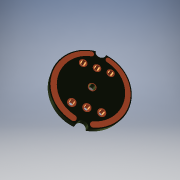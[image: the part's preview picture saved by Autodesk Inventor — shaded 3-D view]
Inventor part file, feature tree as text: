
AUTODESK INVENTOR PART (.ipt)
format: ipt  version: 2016 SP2 (Build 200237200, 237)  size: 261,632 bytes
history: native  units: mm
features: extrude x5, sketch x5, mirror x3, pattern_linear x1
ambient origin geometry x8: Origin, YZ Plane, XZ Plane, XY Plane, X Axis, Y Axis, Z Axis, Center Point
bodies: Solid1 (feature_tree), Solid2 (feature_tree), Solid3 (feature_tree), Solid4 (feature_tree)
feature tree (14):
  extrude  "Extrusion1"  Depth=10.0mm
  extrude  "Extrusion2"  Depth=1.4mm TaperAngle=0.0deg
  extrude  "Extrusion3"  Depth=1.4mm TaperAngle=0.0deg
  pattern_linear  "Rectangular Pattern1"  Count1=3 Spacing1=2.5mm
  mirror  "Mirror1"
  extrude  "Extrusion4"  Depth=1.0mm
  mirror  "Mirror2"
  mirror  "Mirror3"
  extrude  "Extrusion5"  Depth=0.005mm TaperAngle=0.0deg
  sketch  "Sketch1"  dims[d3=1.0mm d4=30.0mm d6=2.5mm d7=10.0mm d9=10.0mm]
  sketch  "Sketch2"  dims[d13=30.0mm d15=10.0mm d16=1.0mm d17=2.5mm d18=1.4mm d19=0.0mm]
  sketch  "Sketch3"  dims[d20=1.2mm d21=1.4mm d22=0.0mm]
  sketch  "Sketch4"  dims[d23=1.5mm]
  sketch  "Sketch5"  dims[d24=0.005mm d25=0.0mm d26=30.0mm d28=2.5mm d29=20.0mm d31=7.5mm d32=1.0mm d33=0.005mm d34=0.0mm d35=1.5mm d36=0.005mm d37=0.0mm]
